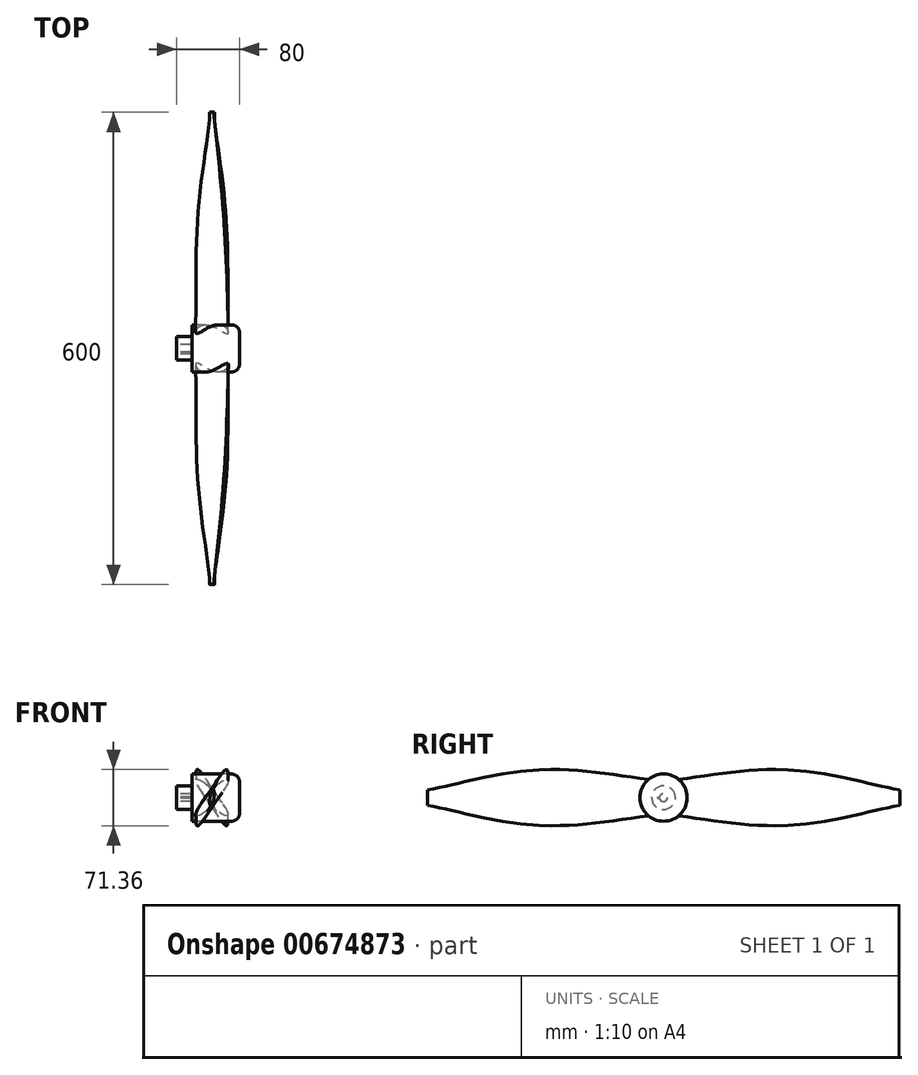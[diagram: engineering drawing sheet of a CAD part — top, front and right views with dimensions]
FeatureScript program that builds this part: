
annotation { "Feature Type Name" : "Feature", "Feature Type Description" : "" }
export const myFeature = defineFeature(function(context is Context, id is Id, definition is map)
    precondition{}
    {
        {
            var Q0;
            Q0=qCreatedBy(makeId("Front.planeOp"),FACE);
            var sketch = newSketch(context, id + "F0", { "sketchPlane" : qUnion([Q0])});
            skEllipse(sketch, "E0", {"center": v(0, 0) * mm, "majorRadius": 30 * mm, "minorRadius": 5 * mm, "majorAxis": v(0.7, 0.7)});
            skLineSegment(sketch, "E1", {"start": v(-21.21, -21.21) * mm, "end": v(21.21, 21.21) * mm, "construction": true});
            skLineSegment(sketch, "E2", {"start": v(-3.54, 3.54) * mm, "end": v(3.54, -3.54) * mm, "construction": true});
            skSolve(sketch);
        }
        {
            assignVariable(context, id + "F1", {"name" : "Amplitude", "anyValue" : 300});
        }
        {
            var Q0;
            Q0=qCreatedBy(makeId("Front.planeOp"),FACE);
            cPlane(context, id + "F2", {"entities" : qUnion([Q0]), "cplaneType" : CPlaneType.OFFSET, "offset" : (getVariable(context, 'Amplitude') / 2) * mm, "width" : 150 * mm, "height" : 150 * mm});
        }
        {
            var Q0;
            Q0=qCreatedBy(id+"F2.planeOp",FACE);
            var sketch = newSketch(context, id + "F3", { "sketchPlane" : qUnion([Q0])});
            skEllipse(sketch, "E3", {"center": v(0, 0) * mm, "majorRadius": 40 * mm, "minorRadius": 5 * mm, "majorAxis": v(0.46, 0.89)});
            skLineSegment(sketch, "E4", {"start": v(-18.47, -35.48) * mm, "end": v(18.47, 35.48) * mm, "construction": true});
            skLineSegment(sketch, "E5", {"start": v(4.44, -2.3) * mm, "end": v(-4.44, 2.3) * mm, "construction": true});
            skSolve(sketch);
        }
        {
            var Q0;
            Q0=qCreatedBy(makeId("Front.planeOp"),FACE);
            cPlane(context, id + "F4", {"entities" : qUnion([Q0]), "cplaneType" : CPlaneType.OFFSET, "offset" : (getVariable(context, 'Amplitude')) * mm, "width" : 150 * mm, "height" : 150 * mm});
        }
        {
            var Q0;
            Q0=qCreatedBy(id+"F4.planeOp",FACE);
            var sketch = newSketch(context, id + "F5", { "sketchPlane" : qUnion([Q0])});
            skEllipse(sketch, "E6", {"center": v(0, 0) * mm, "majorRadius": 10 * mm, "minorRadius": 2.5 * mm, "majorAxis": v(0.17, 0.98)});
            skLineSegment(sketch, "E7", {"start": v(-1.74, -9.85) * mm, "end": v(1.74, 9.85) * mm, "construction": true});
            skLineSegment(sketch, "E8", {"start": v(2.46, -0.43) * mm, "end": v(-2.46, 0.43) * mm, "construction": true});
            skSolve(sketch);
        }
        {
            var Q0;
            Q0 = qSketchRegion(id + "F0", true);
            var Q1;
            Q1 = qSketchRegion(id + "F3", true);
            var Q2;
            Q2 = qSketchRegion(id + "F5", true);
            loft(context, id + "F6", {"sheetProfilesArray" : [{ "sheetProfileEntities" : qUnion([Q0]) }, { "sheetProfileEntities" : qUnion([Q1]) }, { "sheetProfileEntities" : qUnion([Q2]) }]});
        }
        {
            var Q0;
            Q0=qCreatedBy(makeId("Front.planeOp"),FACE);
            var sketch = newSketch(context, id + "F7", { "sketchPlane" : qUnion([Q0])});
            skLineSegment(sketch, "E9", {"start": v(-89.1, 0) * mm, "end": v(108.32, 0) * mm, "construction": true});
            skSolve(sketch);
        }
        {
            var Q0;
            Q0=makeQuery(id+"F6.opLoft","SWEPT_BODY",BODY,{"disambiguationData":[OSD([makeQuery(id+"F0.imprint","IMPRINT",FACE,{"disambiguationData":[TD([[makeQuery(id+"F0.imprint","IMPRINT",EDGE,{"derivedFrom":sQuery(id+"F0.wireOp",EDGE,"E0")}),1.0]])]}),sQuery(id+"F3.wireOp",EDGE,"E3"),makeQuery(id+"F5.imprint","IMPRINT",FACE,{"disambiguationData":[TD([[makeQuery(id+"F5.imprint","IMPRINT",EDGE,{"derivedFrom":sQuery(id+"F5.wireOp",EDGE,"E6")}),1.0]])]})])]});
            var Q1;
            Q1=sQuery(id+"F7.wireOp",EDGE,"E9");
            circularPattern(context, id + "F8", {"entities" : qUnion([Q0]), "axis" : qUnion([Q1]), "angle" : 360 * degree, "instanceCount" : 2, "equalSpace" : true});
        }
        {
            var Q0;
            Q0=qCreatedBy(makeId("Front.planeOp"),FACE);
            var sketch = newSketch(context, id + "F9", { "sketchPlane" : qUnion([Q0])});
            skLineSegment(sketch, "E10", {"start": v(-45, 0) * mm, "end": v(-45, 15) * mm});
            skLineSegment(sketch, "E11", {"start": v(-45, 15) * mm, "end": v(-25, 15) * mm});
            skLineSegment(sketch, "E12", {"start": v(-25, 15) * mm, "end": v(-25, 30) * mm});
            skLineSegment(sketch, "E13", {"start": v(-25, 30) * mm, "end": v(35, 30) * mm});
            skLineSegment(sketch, "E14", {"start": v(35, 30) * mm, "end": v(35, 0) * mm});
            skLineSegment(sketch, "E15", {"start": v(35, 0) * mm, "end": v(-45, 0) * mm});
            skLineSegment(sketch, "E16", {"start": v(-59.6, 0) * mm, "end": v(49.99, 0) * mm, "construction": true});
            skSolve(sketch);
        }
        {
            var Q0;
            Q0 = qSketchRegion(id + "F9", true);
            var Q1;
            Q1=sQuery(id+"F9.wireOp",EDGE,"E16");
            revolve(context, id + "F10", {"operationType" : NewBodyOperationType.ADD, "entities" : qUnion([Q0]), "axis" : qUnion([Q1]), "revolveType" : RevolveType.FULL});
        }
        {
            var Q0;
            Q0=makeQuery(id+"F10.opRevolve","SWEPT_EDGE",EDGE,{"disambiguationData":[OSD([sQuery(id+"F9.wireOp",EDGE,"E13"),sQuery(id+"F9.wireOp",EDGE,"E14")])]});
            fillet(context, id + "F11", {"entities" : qUnion([Q0]), "radius" : 10 * mm, "tangentPropagation" : true, "allowEdgeOverflow" : false});
        }
        {
            var Q0;
            Q0=makeQuery(id+"F10.opRevolve","SWEPT_FACE",FACE,{"disambiguationData":[OSD([sQuery(id+"F9.wireOp",EDGE,"E10")])]});
            var sketch = newSketch(context, id + "F12", { "sketchPlane" : qUnion([Q0])});
            skArc(sketch, "E17", {"start": v(4.9, 1) * mm, "mid": v(-5, 0) * mm, "end": v(4.9, -1) * mm});
            skLineSegment(sketch, "E18.bottom", {"start": v(6.9, -1) * mm, "end": v(4.9, -1) * mm});
            skLineSegment(sketch, "E18.top", {"start": v(6.9, 1) * mm, "end": v(4.9, 1) * mm});
            skLineSegment(sketch, "E18.left", {"start": v(6.9, -1) * mm, "end": v(6.9, 1) * mm});
            skPoint(sketch, "E18.middle", {"position": v(4.78, 0) * mm});
            skPoint(sketch, "E18.right.end.orphan", {"position": v(2.66, 1) * mm});
            skPoint(sketch, "E19.orphan", {"position": v(2.66, -1) * mm});
            skSolve(sketch);
        }
        {
            var Q0;
            Q0 = qSketchRegion(id + "F12", true);
            extrude(context, id + "F13", {"entities" : qUnion([Q0]), "operationType" : NewBodyOperationType.REMOVE, "oppositeDirection" : true, "depth" : 20 * mm, "offsetDistance" : 25 * mm});
        }
    });
